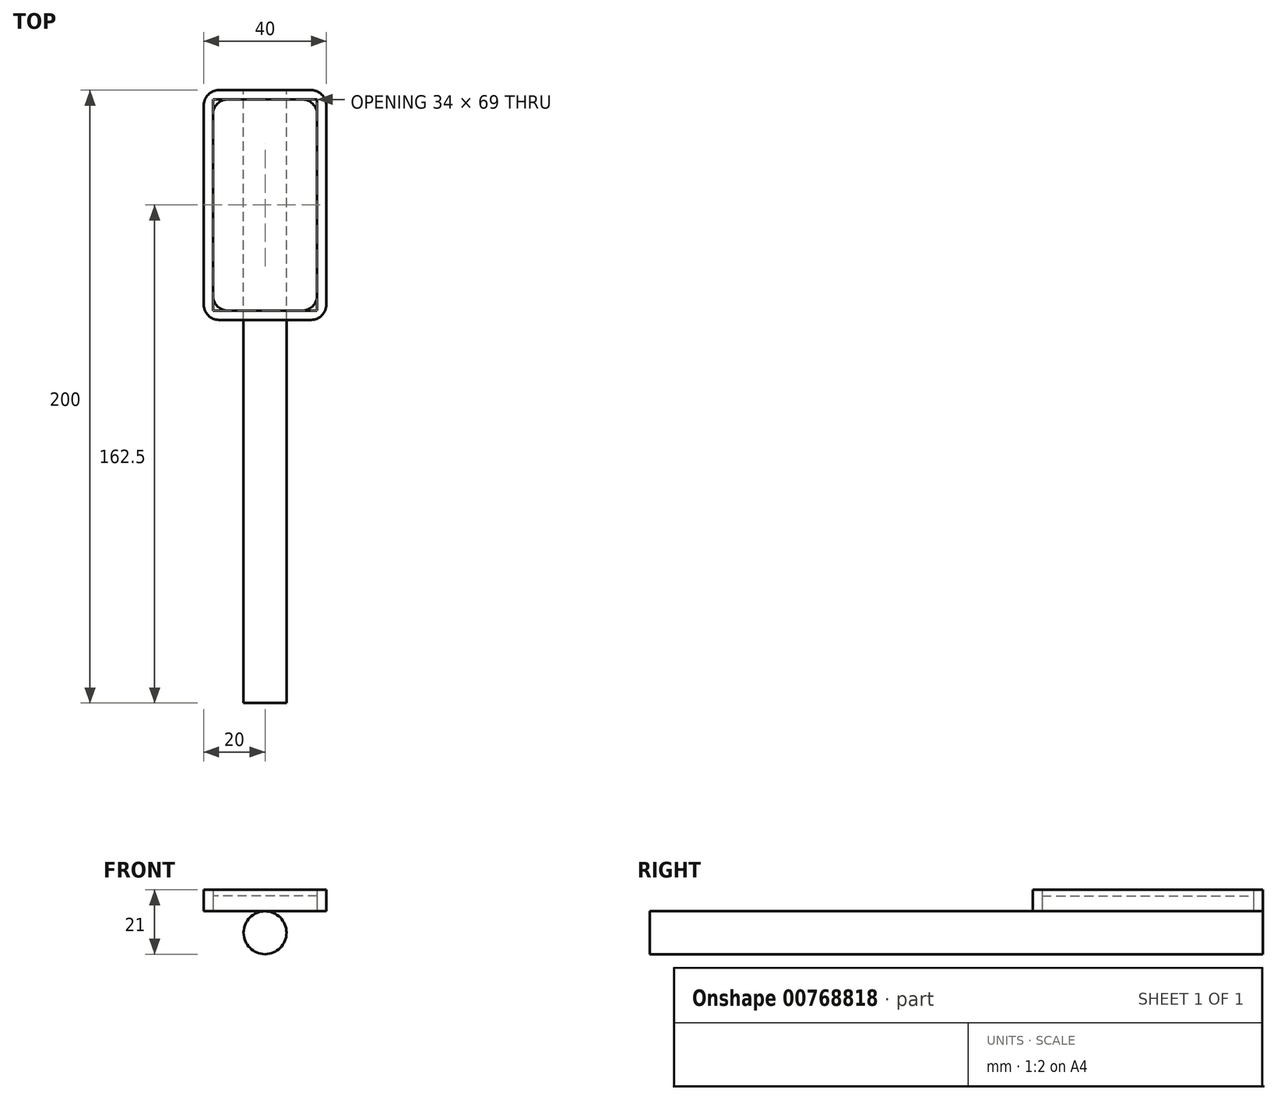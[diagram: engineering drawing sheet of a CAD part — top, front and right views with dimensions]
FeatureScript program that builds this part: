
annotation { "Feature Type Name" : "Feature", "Feature Type Description" : "" }
export const myFeature = defineFeature(function(context is Context, id is Id, definition is map)
    precondition{}
    {
        {
            var Q0;
            Q0=qCreatedBy(makeId("Top.planeOp"),FACE);
            var sketch = newSketch(context, id + "F0", { "sketchPlane" : qUnion([Q0])});
            skLineSegment(sketch, "E0", {"start": v(7, 100) * mm, "end": v(7, -100) * mm});
            skLineSegment(sketch, "E1", {"start": v(7, -100) * mm, "end": v(0, -100) * mm});
            skLineSegment(sketch, "E2", {"start": v(7, 100) * mm, "end": v(0, 100) * mm});
            skLineSegment(sketch, "E3", {"start": v(0, 100) * mm, "end": v(0, -100) * mm});
            skSolve(sketch);
        }
        {
            var Q0;
            Q0=makeQuery(id+"F0.imprint","IMPRINT",FACE,{"disambiguationData":[TD([[makeQuery(id+"F0.imprint","IMPRINT",EDGE,{"derivedFrom":sQuery(id+"F0.wireOp",EDGE,"E0")}),-1.0]])]});
            extrude(context, id + "F1", {"entities" : qUnion([Q0]), "depth" : 7 * mm, "offsetDistance" : 25 * mm});
        }
        {
            var Q0;
            Q0=makeQuery(id+"F0.imprint","IMPRINT",FACE,{"disambiguationData":[TD([[makeQuery(id+"F0.imprint","IMPRINT",EDGE,{"derivedFrom":sQuery(id+"F0.wireOp",EDGE,"E0")}),-1.0]])]});
            var Q1;
            Q1=sQuery(id+"F0.wireOp",EDGE,"E3");
            revolve(context, id + "F2", {"operationType" : NewBodyOperationType.ADD, "surfaceOperationType" : NewSurfaceOperationType.NEW, "entities" : qUnion([Q0]), "axis" : qUnion([Q1]), "revolveType" : RevolveType.FULL});
        }
        {
            var Q0;
            Q0=makeQuery(id+"F1.opExtrude","CAP_EDGE",EDGE,{"disambiguationData":[OSD([sQuery(id+"F0.wireOp",EDGE,"E0")])],"isStart":false});
            fillet(context, id + "F3", {"entities" : qUnion([Q0]), "radius" : 7 * mm, "tangentPropagation" : true, "allowEdgeOverflow" : false});
        }
        {
            var Q0;
            Q0=qCreatedBy(makeId("Top.planeOp"),FACE);
            cPlane(context, id + "F4", {"entities" : qUnion([Q0]), "cplaneType" : CPlaneType.OFFSET, "offset" : 7 * mm, "width" : 150 * mm, "height" : 150 * mm});
        }
        {
            var Q0;
            Q0=qCreatedBy(id+"F4.planeOp",FACE);
            var sketch = newSketch(context, id + "F5", { "sketchPlane" : qUnion([Q0])});
            skLineSegment(sketch, "E4.top", {"start": v(20, 100) * mm, "end": v(-20, 100) * mm});
            skPoint(sketch, "E5.oppositeSnap0", {"position": v(-17, 37.5) * mm});
            skLineSegment(sketch, "E6", {"start": v(20, 100) * mm, "end": v(20, 25) * mm});
            skLineSegment(sketch, "E7.bottom", {"start": v(20, 25) * mm, "end": v(-20, 25) * mm});
            skLineSegment(sketch, "E7.left", {"start": v(20, 25) * mm, "end": v(20, 100) * mm});
            skLineSegment(sketch, "E7.right", {"start": v(-20, 25) * mm, "end": v(-20, 100) * mm});
            skLineSegment(sketch, "E8.bottom", {"start": v(17, 28) * mm, "end": v(-17, 28) * mm});
            skLineSegment(sketch, "E8.top", {"start": v(17, 97) * mm, "end": v(-17, 97) * mm});
            skLineSegment(sketch, "E8.left", {"start": v(17, 28) * mm, "end": v(17, 97) * mm});
            skLineSegment(sketch, "E8.right", {"start": v(-17, 28) * mm, "end": v(-17, 97) * mm});
            skSolve(sketch);
        }
        {
            var Q0;
            Q0=makeQuery(id+"F5.imprint","IMPRINT",FACE,{"disambiguationData":[TD([[makeQuery(id+"F5.imprint","IMPRINT",EDGE,{"derivedFrom":sQuery(id+"F5.wireOp",EDGE,"E8.bottom")}),-1.0]])]});
            extrude(context, id + "F6", {"entities" : qUnion([Q0]), "operationType" : NewBodyOperationType.ADD, "depth" : 5 * mm, "offsetDistance" : 25 * mm});
        }
        {
            var Q0;
            Q0=makeQuery(id+"F5.imprint","IMPRINT",FACE,{"disambiguationData":[TD([[makeQuery(id+"F5.imprint","IMPRINT",EDGE,{"derivedFrom":sQuery(id+"F5.wireOp",EDGE,"E4.top")}),1.0]])]});
            extrude(context, id + "F7", {"entities" : qUnion([Q0]), "depth" : 7 * mm, "offsetDistance" : 25 * mm});
        }
        {
            var Q0;
            Q0=makeQuery(id+"F7.opExtrude","SWEPT_EDGE",EDGE,{"disambiguationData":[OSD([sQuery(id+"F5.wireOp",EDGE,"E8.top"),sQuery(id+"F5.wireOp",EDGE,"E8.right")])]});
            var Q1;
            Q1=makeQuery(id+"F7.opExtrude","SWEPT_EDGE",EDGE,{"disambiguationData":[OSD([sQuery(id+"F5.wireOp",EDGE,"E8.bottom"),sQuery(id+"F5.wireOp",EDGE,"E8.left")])]});
            var Q2;
            Q2=makeQuery(id+"F7.opExtrude","SWEPT_EDGE",EDGE,{"disambiguationData":[OSD([sQuery(id+"F5.wireOp",EDGE,"E8.bottom"),sQuery(id+"F5.wireOp",EDGE,"E8.right")])]});
            fillet(context, id + "F8", {"entities" : qUnion([Q0, Q1, Q2]), "radius" : 5 * mm, "tangentPropagation" : true, "allowEdgeOverflow" : false});
        }
        {
            var Q0;
            Q0=makeQuery(id+"F7.opExtrude","SWEPT_EDGE",EDGE,{"disambiguationData":[OSD([sQuery(id+"F5.wireOp",EDGE,"E8.top"),sQuery(id+"F5.wireOp",EDGE,"E8.left")])]});
            fillet(context, id + "F9", {"entities" : qUnion([Q0]), "radius" : 5 * mm, "tangentPropagation" : true, "allowEdgeOverflow" : false});
        }
        {
            var Q0;
            Q0=makeQuery(id+"F7.opExtrude","SWEPT_EDGE",EDGE,{"disambiguationData":[OSD([sQuery(id+"F5.wireOp",EDGE,"E7.bottom"),sQuery(id+"F5.wireOp",EDGE,"E7.right")])]});
            var Q1;
            Q1=makeQuery(id+"F7.opExtrude","SWEPT_EDGE",EDGE,{"disambiguationData":[OSD([sQuery(id+"F5.wireOp",EDGE,"E7.bottom"),sQuery(id+"F5.wireOp",EDGE,"E7.left")])]});
            fillet(context, id + "F10", {"entities" : qUnion([Q0, Q1]), "radius" : 5 * mm, "tangentPropagation" : true, "allowEdgeOverflow" : false});
        }
        {
            var Q0;
            Q0=makeQuery(id+"F7.opExtrude","SWEPT_EDGE",EDGE,{"disambiguationData":[OSD([sQuery(id+"F5.wireOp",EDGE,"E4.top"),sQuery(id+"F5.wireOp",EDGE,"E7.left")])]});
            var Q1;
            Q1=makeQuery(id+"F7.opExtrude","SWEPT_EDGE",EDGE,{"disambiguationData":[OSD([sQuery(id+"F5.wireOp",EDGE,"E4.top"),sQuery(id+"F5.wireOp",EDGE,"E7.right")])]});
            fillet(context, id + "F11", {"entities" : qUnion([Q0, Q1]), "radius" : 5 * mm, "tangentPropagation" : true, "allowEdgeOverflow" : false});
        }
    });
